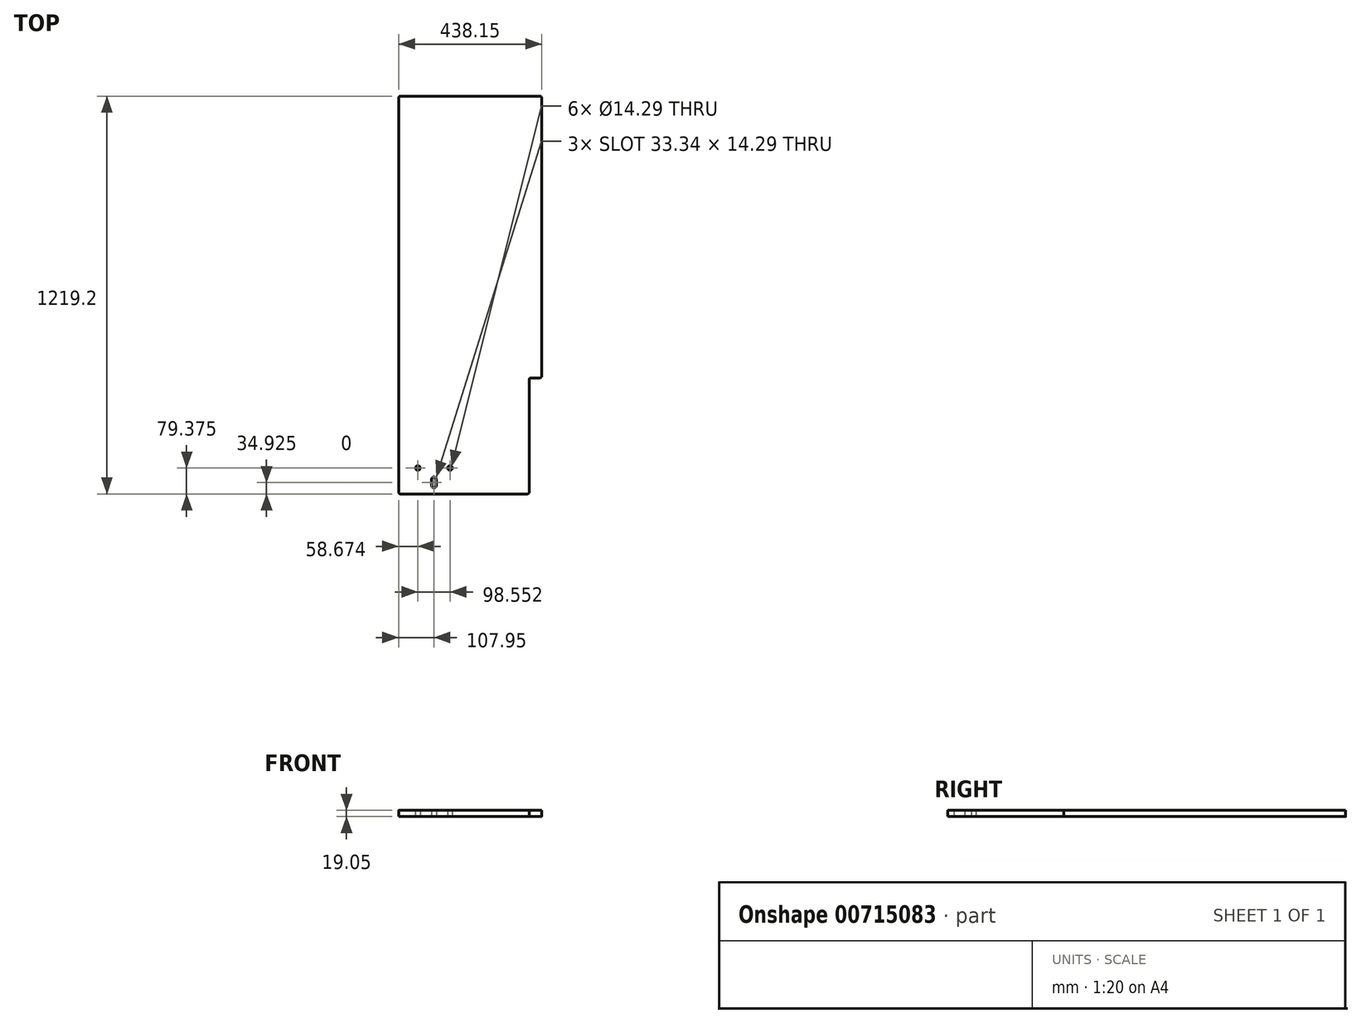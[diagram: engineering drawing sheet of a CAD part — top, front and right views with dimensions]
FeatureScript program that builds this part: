
annotation { "Feature Type Name" : "Feature", "Feature Type Description" : "" }
export const myFeature = defineFeature(function(context is Context, id is Id, definition is map)
    precondition{}
    {
        {
            var Q0;
            Q0=qCreatedBy(makeId("Top.planeOp"),FACE);
            var sketch = newSketch(context, id + "F0", { "sketchPlane" : qUnion([Q0])});
            skLineSegment(sketch, "E0.bottom", {"start": v(0, 0) * mm, "end": v(400.05, 0) * mm});
            skLineSegment(sketch, "E0.top", {"start": v(0, 1219.2) * mm, "end": v(438.15, 1219.2) * mm});
            skLineSegment(sketch, "E0.left", {"start": v(0, 0) * mm, "end": v(0, 1219.2) * mm});
            skLineSegment(sketch, "E0.right", {"start": v(438.15, 355.6) * mm, "end": v(438.15, 1219.2) * mm});
            skLineSegment(sketch, "E1.top", {"start": v(438.15, 355.6) * mm, "end": v(400.05, 355.6) * mm});
            skLineSegment(sketch, "E1.right", {"start": v(400.05, 0) * mm, "end": v(400.05, 355.6) * mm});
            skLineSegment(sketch, "E2.bottom", {"start": v(406.4, 1067.06) * mm, "end": v(76.2, 1067.06) * mm, "construction": true});
            skLineSegment(sketch, "E2.top", {"start": v(406.4, 505.7) * mm, "end": v(76.2, 505.7) * mm, "construction": true});
            skLineSegment(sketch, "E2.left", {"start": v(406.4, 1067.06) * mm, "end": v(406.4, 505.7) * mm, "construction": true});
            skLineSegment(sketch, "E2.right", {"start": v(76.2, 1067.06) * mm, "end": v(76.2, 505.7) * mm, "construction": true});
            skLineSegment(sketch, "E3", {"start": v(107.95, 1067.06) * mm, "end": v(107.95, 79.37) * mm, "construction": true});
            skLineSegment(sketch, "E4", {"start": v(241.3, 505.7) * mm, "end": v(241.3, 1198.88) * mm, "construction": true});
            skLineSegment(sketch, "E5", {"start": v(58.67, 79.37) * mm, "end": v(157.23, 79.38) * mm, "construction": true});
            skCircle(sketch, "E6", {"center": v(58.67, 79.37) * mm, "radius": 7.14 * mm});
            skCircle(sketch, "E7", {"center": v(157.23, 79.37) * mm, "radius": 7.14 * mm});
            skLineSegment(sketch, "E8.left", {"start": v(115.1, 25.4) * mm, "end": v(115.1, 44.45) * mm});
            skLineSegment(sketch, "E8.right", {"start": v(100.8, 25.4) * mm, "end": v(100.8, 44.45) * mm});
            skPoint(sketch, "E8.middle", {"position": v(107.95, 34.93) * mm});
            skArc(sketch, "E9", {"start": v(100.8, 25.4) * mm, "mid": v(107.95, 18.26) * mm, "end": v(115.1, 25.4) * mm});
            skArc(sketch, "E10", {"start": v(115.1, 44.45) * mm, "mid": v(107.95, 51.6) * mm, "end": v(100.8, 44.45) * mm});
            skLineSegment(sketch, "E11", {"start": v(0, 25.06) * mm, "end": v(187.7, 25.06) * mm, "construction": true});
            skLineSegment(sketch, "E12", {"start": v(107.95, 79.38) * mm, "end": v(107.95, 34.93) * mm, "construction": true});
            skSolve(sketch);
        }
        {
            var Q0;
            Q0 = qSketchRegion(id + "F0", true);
            extrude(context, id + "F1", {"entities" : qUnion([Q0]), "depth" : 19.05 * mm, "offsetDistance" : 25.4 * mm});
        }
        {
            var Q0;
            Q0=makeQuery(id+"F1.opExtrude","SWEPT_EDGE",EDGE,{"disambiguationData":[OSD([sQuery(id+"F0.wireOp",EDGE,"E0.top"),sQuery(id+"F0.wireOp",EDGE,"E0.left")])]});
            var Q1;
            Q1=makeQuery(id+"F1.opExtrude","SWEPT_EDGE",EDGE,{"disambiguationData":[OSD([sQuery(id+"F0.wireOp",EDGE,"E0.bottom"),sQuery(id+"F0.wireOp",EDGE,"E0.left")])]});
            var Q2;
            Q2=makeQuery(id+"F1.opExtrude","SWEPT_EDGE",EDGE,{"disambiguationData":[OSD([sQuery(id+"F0.wireOp",EDGE,"E0.right"),sQuery(id+"F0.wireOp",EDGE,"E1.top")])]});
            var Q3;
            Q3=makeQuery(id+"F1.opExtrude","SWEPT_EDGE",EDGE,{"disambiguationData":[OSD([sQuery(id+"F0.wireOp",EDGE,"E0.bottom"),sQuery(id+"F0.wireOp",EDGE,"E1.right")])]});
            var Q4;
            Q4=makeQuery(id+"F1.opExtrude","SWEPT_EDGE",EDGE,{"disambiguationData":[OSD([sQuery(id+"F0.wireOp",EDGE,"E1.top"),sQuery(id+"F0.wireOp",EDGE,"E1.right")])]});
            var Q5;
            Q5=makeQuery(id+"F1.opExtrude","SWEPT_EDGE",EDGE,{"disambiguationData":[OSD([sQuery(id+"F0.wireOp",EDGE,"E0.top"),sQuery(id+"F0.wireOp",EDGE,"E0.right")])]});
            fillet(context, id + "F2", {"entities" : qUnion([Q0, Q1, Q2, Q3, Q4, Q5]), "radius" : 5.08 * mm, "tangentPropagation" : true, "allowEdgeOverflow" : false});
        }
    });
